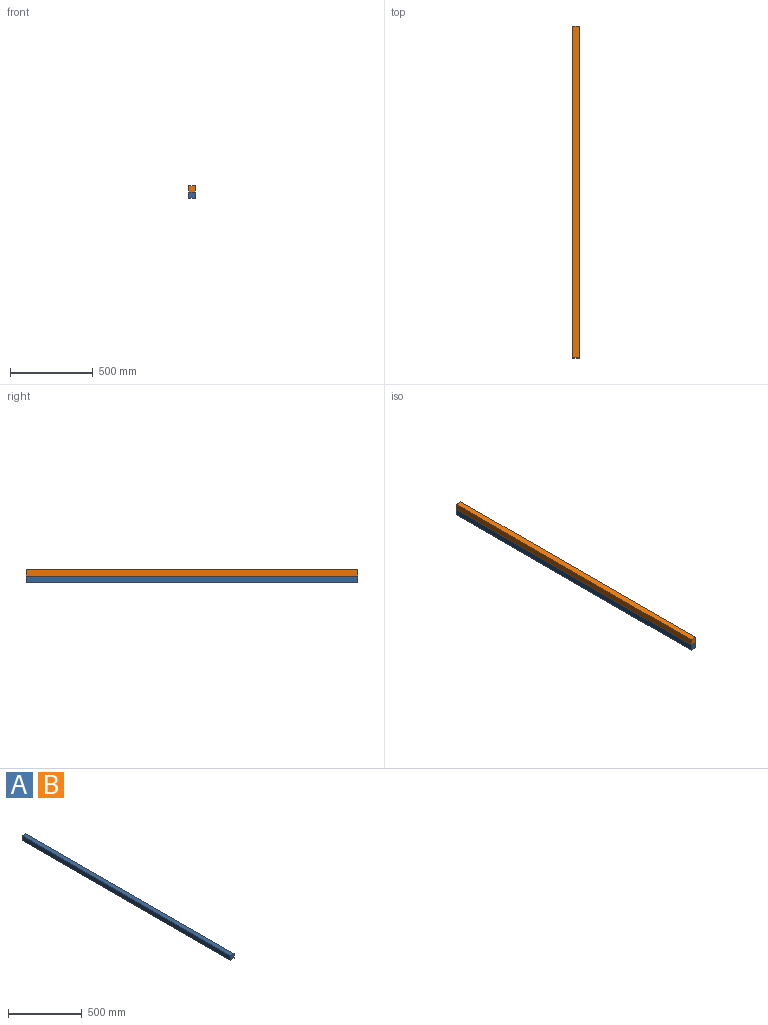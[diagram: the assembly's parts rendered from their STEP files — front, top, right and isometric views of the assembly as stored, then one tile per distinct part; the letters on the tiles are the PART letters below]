
ASSEMBLY  parts=2 mates=1
PART A: 6 faces, bbox 38.1x2000x38.1 mm
  f0: plane 38.1x38.1mm, normal (0,1,0), area 1451.6mm2, adj f1,f3,f4,f5
  f1: plane 2000x38.1mm, normal (1,0,0), area 76200mm2, adj f0,f2,f3,f4
  f2: plane 38.1x38.1mm, normal (0,-1,0), area 1451.6mm2, adj f1,f3,f4,f5
  f3: plane 2000x38.1mm, normal (0,0,-1), area 76200mm2, adj f0,f1,f2,f5
  f4: plane 2000x38.1mm, normal (0,0,1), area 76200mm2, adj f0,f1,f2,f5
  f5: plane 2000x38.1mm, normal (-1,0,0), area 76200mm2, adj f0,f2,f3,f4
PART B: same geometry as A
PLACE A t=(-483.08,-529.26,179.34)mm
PLACE B t=(-483.08,-529.26,217.44)mm
MATE fastened A.f4 <-> B.f3  axis (0,0,1) through (103.89,-529.26,217.44)mm
